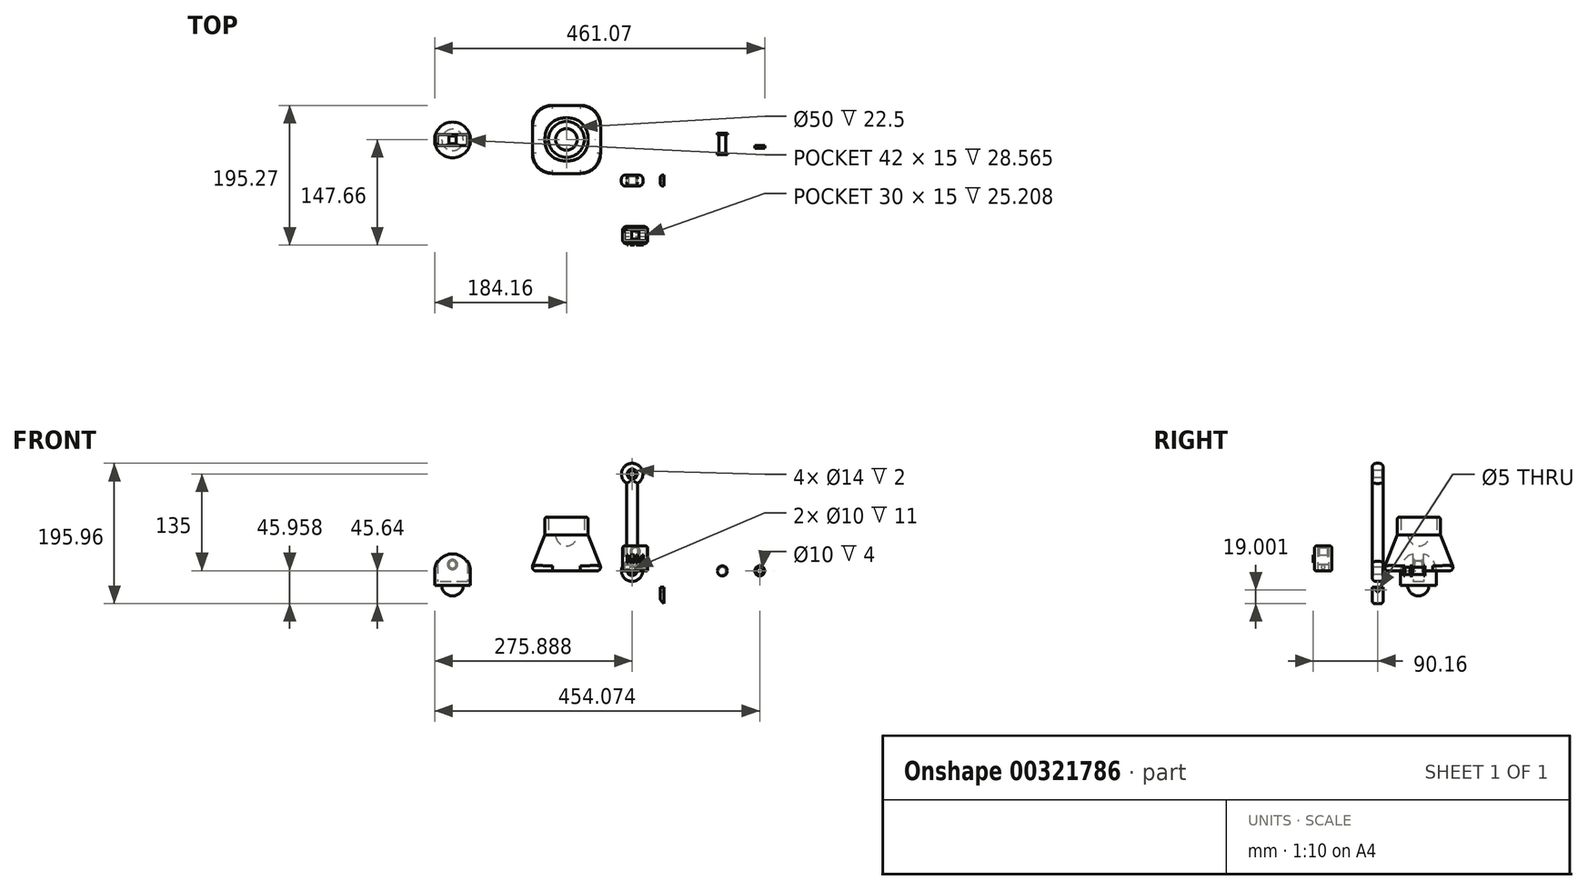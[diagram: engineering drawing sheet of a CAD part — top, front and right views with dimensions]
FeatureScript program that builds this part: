
annotation { "Feature Type Name" : "Feature", "Feature Type Description" : "" }
export const myFeature = defineFeature(function(context is Context, id is Id, definition is map)
    precondition{}
    {
        {
            var Q0;
            Q0=qCreatedBy(makeId("Top.planeOp"),FACE);
            var sketch = newSketch(context, id + "F0", { "sketchPlane" : qUnion([Q0])});
            skLineSegment(sketch, "E0.bottom", {"start": v(0, 0) * mm, "end": v(100, 0) * mm});
            skLineSegment(sketch, "E0.top", {"start": v(0, 100) * mm, "end": v(100, 100) * mm});
            skLineSegment(sketch, "E0.left", {"start": v(0, 0) * mm, "end": v(0, 100) * mm});
            skLineSegment(sketch, "E0.right", {"start": v(100, 0) * mm, "end": v(100, 100) * mm});
            skSolve(sketch);
        }
        {
            var Q0;
            Q0=makeQuery(id+"F0.imprint","IMPRINT",FACE,{"disambiguationData":[TD([[makeQuery(id+"F0.imprint","IMPRINT",EDGE,{"derivedFrom":sQuery(id+"F0.wireOp",EDGE,"E0.bottom")}),1.0]])]});
            cPlane(context, id + "F1", {"entities" : qUnion([Q0]), "cplaneType" : CPlaneType.OFFSET, "offset" : 50 * mm, "width" : 150 * mm, "height" : 150 * mm});
        }
        {
            var Q0;
            Q0=qCreatedBy(id+"F1.planeOp",FACE);
            var sketch = newSketch(context, id + "F2", { "sketchPlane" : qUnion([Q0])});
            skLineSegment(sketch, "E1.bottom", {"start": v(20, 80) * mm, "end": v(80, 80) * mm});
            skLineSegment(sketch, "E1.top", {"start": v(20, 20) * mm, "end": v(80, 20) * mm});
            skLineSegment(sketch, "E1.left", {"start": v(20, 80) * mm, "end": v(20, 20) * mm});
            skLineSegment(sketch, "E1.right", {"start": v(80, 80) * mm, "end": v(80, 20) * mm});
            skSolve(sketch);
        }
        {
            var Q0;
            Q0=makeQuery(id+"F0.imprint","IMPRINT",FACE,{"disambiguationData":[TD([[makeQuery(id+"F0.imprint","IMPRINT",EDGE,{"derivedFrom":sQuery(id+"F0.wireOp",EDGE,"E0.bottom")}),1.0]])]});
            var Q1;
            Q1=makeQuery(id+"F2.imprint","IMPRINT",FACE,{"disambiguationData":[TD([[makeQuery(id+"F2.imprint","IMPRINT",EDGE,{"derivedFrom":sQuery(id+"F2.wireOp",EDGE,"E1.bottom")}),-1.0]])]});
            loft(context, id + "F3", {"sheetProfilesArray" : [{ "sheetProfileEntities" : qUnion([Q0]) }, { "sheetProfileEntities" : qUnion([Q1]) }]});
        }
        {
            var Q0;
            Q0=makeQuery(id+"F3.opLoft","CAP_FACE",FACE,{"disambiguationData":[OSD([makeQuery(id+"F2.imprint","IMPRINT",FACE,{"disambiguationData":[TD([[makeQuery(id+"F2.imprint","IMPRINT",EDGE,{"derivedFrom":sQuery(id+"F2.wireOp",EDGE,"E1.bottom")}),-1.0]])]})])],"isStart":true});
            var sketch = newSketch(context, id + "F4", { "sketchPlane" : qUnion([Q0])});
            skLineSegment(sketch, "E2", {"start": v(50, 65) * mm, "end": v(50, 35) * mm});
            skArc(sketch, "E3", {"start": v(50, 35) * mm, "mid": v(65, 50) * mm, "end": v(50, 65) * mm});
            skPoint(sketch, "E4.orphan", {"position": v(50, 80) * mm});
            skPoint(sketch, "E5.orphan", {"position": v(50, 20) * mm});
            skSolve(sketch);
        }
        {
            var Q0;
            Q0=makeQuery(id+"F4.imprint","IMPRINT",FACE,{"disambiguationData":[TD([[makeQuery(id+"F4.imprint","IMPRINT",EDGE,{"derivedFrom":sQuery(id+"F4.wireOp",EDGE,"E2")}),1.0]])]});
            var Q1;
            Q1=sQuery(id+"F4.wireOp",EDGE,"E2");
            revolve(context, id + "F5", {"operationType" : NewBodyOperationType.REMOVE, "entities" : qUnion([Q0]), "axis" : qUnion([Q1]), "revolveType" : RevolveType.FULL, "oppositeDirection" : true});
        }
        {
            var Q0;
            Q0=makeQuery(id+"F3.opLoft","CAP_FACE",FACE,{"disambiguationData":[OSD([makeQuery(id+"F0.imprint","IMPRINT",FACE,{"disambiguationData":[TD([[makeQuery(id+"F0.imprint","IMPRINT",EDGE,{"derivedFrom":sQuery(id+"F0.wireOp",EDGE,"E0.bottom")}),1.0]])]})])],"isStart":true});
            fillet(context, id + "F6", {"entities" : qUnion([Q0]), "radius" : 5 * mm, "tangentPropagation" : true, "allowEdgeOverflow" : false});
        }
        {
            var Q0;
            Q0=makeQuery(id+"F3.opLoft","SWEPT_EDGE",EDGE,{"disambiguationData":[OSD([sQuery(id+"F0.wireOp",EDGE,"E0.bottom"),sQuery(id+"F0.wireOp",EDGE,"E0.right"),sQuery(id+"F2.wireOp",EDGE,"E1.top"),sQuery(id+"F2.wireOp",EDGE,"E1.right")])]});
            var Q1;
            Q1=makeQuery(id+"F3.opLoft","SWEPT_EDGE",EDGE,{"disambiguationData":[OSD([sQuery(id+"F0.wireOp",EDGE,"E0.top"),sQuery(id+"F0.wireOp",EDGE,"E0.right"),sQuery(id+"F2.wireOp",EDGE,"E1.bottom"),sQuery(id+"F2.wireOp",EDGE,"E1.right")])]});
            var Q2;
            Q2=makeQuery(id+"F3.opLoft","SWEPT_EDGE",EDGE,{"disambiguationData":[OSD([sQuery(id+"F0.wireOp",EDGE,"E0.top"),sQuery(id+"F0.wireOp",EDGE,"E0.left"),sQuery(id+"F2.wireOp",EDGE,"E1.bottom"),sQuery(id+"F2.wireOp",EDGE,"E1.left")])]});
            var Q3;
            Q3=makeQuery(id+"F3.opLoft","SWEPT_EDGE",EDGE,{"disambiguationData":[OSD([sQuery(id+"F0.wireOp",EDGE,"E0.bottom"),sQuery(id+"F0.wireOp",EDGE,"E0.left"),sQuery(id+"F2.wireOp",EDGE,"E1.top"),sQuery(id+"F2.wireOp",EDGE,"E1.left")])]});
            fillet(context, id + "F7", {"entities" : qUnion([Q0, Q1, Q2, Q3]), "radius" : 30 * mm, "tangentPropagation" : true, "allowEdgeOverflow" : false});
        }
        {
            var Q0;
            Q0=qCreatedBy(makeId("Top.planeOp"),FACE);
            var sketch = newSketch(context, id + "F8", { "sketchPlane" : qUnion([Q0])});
            skArc(sketch, "E6", {"start": v(184.89, 22.61) * mm, "mid": v(199.89, 37.61) * mm, "end": v(184.89, 52.61) * mm});
            skLineSegment(sketch, "E7", {"start": v(184.89, 22.61) * mm, "end": v(184.89, 52.61) * mm});
            skSolve(sketch);
        }
        {
            var Q0;
            Q0=qCreatedBy(makeId("Top.planeOp"),FACE);
            cPlane(context, id + "F9", {"entities" : qUnion([Q0]), "cplaneType" : CPlaneType.OFFSET, "offset" : 10 * mm, "width" : 150 * mm, "height" : 150 * mm});
        }
        {
            var Q0;
            Q0=qCreatedBy(id+"F9.planeOp",FACE);
            var sketch = newSketch(context, id + "F10", { "sketchPlane" : qUnion([Q0])});
            skLineSegment(sketch, "E8.bottom", {"start": v(177.39, 45.11) * mm, "end": v(192.39, 45.11) * mm});
            skLineSegment(sketch, "E8.top", {"start": v(177.39, 30.11) * mm, "end": v(192.39, 30.11) * mm});
            skLineSegment(sketch, "E8.left", {"start": v(177.39, 45.11) * mm, "end": v(177.39, 30.11) * mm});
            skLineSegment(sketch, "E8.right", {"start": v(192.39, 45.11) * mm, "end": v(192.39, 30.11) * mm});
            skSolve(sketch);
        }
        {
            var Q0;
            Q0=makeQuery(id+"F8.imprint","IMPRINT",FACE,{"disambiguationData":[TD([[makeQuery(id+"F8.imprint","IMPRINT",EDGE,{"derivedFrom":sQuery(id+"F8.wireOp",EDGE,"E6")}),1.0]])]});
            var Q1;
            Q1=sQuery(id+"F8.wireOp",EDGE,"E7");
            revolve(context, id + "F11", {"entities" : qUnion([Q0]), "axis" : qUnion([Q1]), "revolveType" : RevolveType.FULL});
        }
        {
            var Q0;
            Q0=qSketchRegion(id+"F10",true);
            extrude(context, id + "F12", {"entities" : qUnion([Q0]), "operationType" : NewBodyOperationType.ADD, "depth" : 120 * mm});
        }
        {
            var Q0;
            Q0=makeQuery(id+"F12.boolean.opBoolean","INTERSECT",EDGE,{"derivedFrom":[makeQuery(id+"F11.opRevolve","SWEPT_FACE",FACE,{"disambiguationData":[OSD([sQuery(id+"F8.wireOp",EDGE,"E6")])]}),makeQuery(id+"F12.opExtrude","SWEPT_FACE",FACE,{"disambiguationData":[OSD([sQuery(id+"F10.wireOp",EDGE,"E8.right")])]})]});
            var Q1;
            Q1=makeQuery(id+"F12.boolean.opBoolean","INTERSECT",EDGE,{"derivedFrom":[makeQuery(id+"F11.opRevolve","SWEPT_FACE",FACE,{"disambiguationData":[OSD([sQuery(id+"F8.wireOp",EDGE,"E6")])]}),makeQuery(id+"F12.opExtrude","SWEPT_FACE",FACE,{"disambiguationData":[OSD([sQuery(id+"F10.wireOp",EDGE,"E8.top")])]})]});
            var Q2;
            Q2=makeQuery(id+"F12.boolean.opBoolean","INTERSECT",EDGE,{"derivedFrom":[makeQuery(id+"F11.opRevolve","SWEPT_FACE",FACE,{"disambiguationData":[OSD([sQuery(id+"F8.wireOp",EDGE,"E6")])]}),makeQuery(id+"F12.opExtrude","SWEPT_FACE",FACE,{"disambiguationData":[OSD([sQuery(id+"F10.wireOp",EDGE,"E8.bottom")])]})]});
            var Q3;
            Q3=makeQuery(id+"F12.boolean.opBoolean","INTERSECT",EDGE,{"derivedFrom":[makeQuery(id+"F11.opRevolve","SWEPT_FACE",FACE,{"disambiguationData":[OSD([sQuery(id+"F8.wireOp",EDGE,"E6")])]}),makeQuery(id+"F12.opExtrude","SWEPT_FACE",FACE,{"disambiguationData":[OSD([sQuery(id+"F10.wireOp",EDGE,"E8.left")])]})]});
            var Q4;
            Q4=makeQuery(id+"F12.opExtrude","SWEPT_EDGE",EDGE,{"disambiguationData":[OSD([sQuery(id+"F10.wireOp",EDGE,"E8.bottom"),sQuery(id+"F10.wireOp",EDGE,"E8.left")])]});
            var Q5;
            Q5=makeQuery(id+"F12.opExtrude","SWEPT_EDGE",EDGE,{"disambiguationData":[OSD([sQuery(id+"F10.wireOp",EDGE,"E8.bottom"),sQuery(id+"F10.wireOp",EDGE,"E8.right")])]});
            var Q6;
            Q6=makeQuery(id+"F12.opExtrude","SWEPT_EDGE",EDGE,{"disambiguationData":[OSD([sQuery(id+"F10.wireOp",EDGE,"E8.top"),sQuery(id+"F10.wireOp",EDGE,"E8.right")])]});
            var Q7;
            Q7=makeQuery(id+"F12.opExtrude","SWEPT_EDGE",EDGE,{"disambiguationData":[OSD([sQuery(id+"F10.wireOp",EDGE,"E8.top"),sQuery(id+"F10.wireOp",EDGE,"E8.left")])]});
            fillet(context, id + "F13", {"entities" : qUnion([Q0, Q1, Q2, Q3, Q4, Q5, Q6, Q7]), "radius" : 5 * mm, "tangentPropagation" : true, "allowEdgeOverflow" : false});
        }
        {
            var Q0;
            Q0=makeQuery(id+"F12.opExtrude","CAP_EDGE",EDGE,{"disambiguationData":[OSD([sQuery(id+"F10.wireOp",EDGE,"E8.right")])],"isStart":false});
            cPoint(context, id + "F14", {"entities" : qUnion([Q0]), "parameter" : 0.5});
        }
        {
            var Q0;
            Q0=makeQuery(id+"F12.opExtrude","CAP_EDGE",EDGE,{"disambiguationData":[OSD([sQuery(id+"F10.wireOp",EDGE,"E8.left")])],"isStart":false});
            cPoint(context, id + "F15", {"entities" : qUnion([Q0]), "parameter" : 0.5});
        }
        {
            var Q0;
            {var subQ0=makeQuery(id+"F12.opExtrude","SWEPT_FACE",FACE,{"disambiguationData":[OSD([sQuery(id+"F10.wireOp",EDGE,"E8.left")])]});Q0=makeQuery(id+"F13.opFillet","BLEND_EDGE",EDGE,{"blendedFrom":[makeQuery(id+"F12.boolean.opBoolean","INTERSECT",EDGE,{"derivedFrom":[makeQuery(id+"F11.opRevolve","SWEPT_FACE",FACE,{"disambiguationData":[OSD([sQuery(id+"F8.wireOp",EDGE,"E6")])]}),subQ0]}),subQ0],"blendedInto":[subQ0]});}
            cPoint(context, id + "F16", {"entities" : qUnion([Q0]), "parameter" : 0.5});
        }
        {
            var Q0;
            Q0=qCreatedBy(id+"F14",VERTEX);
            var Q1;
            Q1=qCreatedBy(id+"F15",VERTEX);
            var Q2;
            Q2=qCreatedBy(id+"F16",VERTEX);
            cPlane(context, id + "F17", {"entities" : qUnion([Q0, Q1, Q2]), "cplaneType" : CPlaneType.THREE_POINT, "offset" : 25 * mm, "width" : 150 * mm, "height" : 150 * mm});
        }
        {
            var Q0;
            Q0=qCreatedBy(id+"F17.planeOp",FACE);
            var sketch = newSketch(context, id + "F18", { "sketchPlane" : qUnion([Q0])});
            skCircle(sketch, "E9", {"center": v(-184.89, 137.5) * mm, "radius": 15 * mm});
            skSolve(sketch);
        }
        {
            var Q0;
            Q0=makeQuery(id+"F18.imprint","IMPRINT",FACE,{"disambiguationData":[TD([[makeQuery(id+"F18.imprint","IMPRINT",EDGE,{"derivedFrom":sQuery(id+"F18.wireOp",EDGE,"E9")}),1.0]])]});
            extrude(context, id + "F19", {"entities" : qUnion([Q0]), "operationType" : NewBodyOperationType.ADD, "endBound" : BoundingType.SYMMETRIC, "depth" : 15 * mm});
        }
        {
            var Q0;
            Q0=makeQuery(id+"F19.opExtrude","CAP_EDGE",EDGE,{"disambiguationData":[OSD([sQuery(id+"F18.wireOp",EDGE,"E9")])],"isStart":true});
            var Q1;
            Q1=makeQuery(id+"F19.opExtrude","CAP_EDGE",EDGE,{"disambiguationData":[OSD([sQuery(id+"F18.wireOp",EDGE,"E9")])],"isStart":false});
            fillet(context, id + "F20", {"entities" : qUnion([Q0, Q1]), "radius" : 5 * mm, "tangentPropagation" : true, "allowEdgeOverflow" : false});
        }
        {
            var Q0;
            Q0=makeQuery(id+"F19.boolean.opBoolean","MERGE",FACE,{"derivedFrom":[makeQuery(id+"F12.opExtrude","SWEPT_FACE",FACE,{"disambiguationData":[OSD([sQuery(id+"F10.wireOp",EDGE,"E8.top")])]}),makeQuery(id+"F19.opExtrude","CAP_FACE",FACE,{"disambiguationData":[OSD([sQuery(id+"F18.wireOp",EDGE,"E9")])],"isStart":true})]});
            var sketch = newSketch(context, id + "F21", { "sketchPlane" : qUnion([Q0])});
            skCircle(sketch, "E10", {"center": v(184.89, 137.5) * mm, "radius": 5 * mm});
            skCircle(sketch, "E11", {"center": v(184.89, 137.5) * mm, "radius": 7 * mm});
            skSolve(sketch);
        }
        {
            var Q0;
            Q0=sQuery(id+"F21.wireOp",VERTEX,"E10.center");
            var Q1;
            Q1=makeQuery(id+"F11.opRevolve","SWEPT_BODY",BODY,{"disambiguationData":[OSD([sQuery(id+"F8.wireOp",EDGE,"E6"),sQuery(id+"F8.wireOp",EDGE,"E7")])]});
            hole(context, id + "F22", {"style" : HoleStyle.SIMPLE, "endStyle" : HoleEndStyle.THROUGH, "holeDiameter" : 10 * mm, "tappedDepth" : 12 * mm, "tapClearance" : 3, "locations" : qUnion([Q0]), "scope" : qUnion([Q1])});
        }
        {
            var Q0;
            Q0=makeQuery(id+"F19.boolean.opBoolean","MERGE",FACE,{"derivedFrom":[makeQuery(id+"F12.opExtrude","SWEPT_FACE",FACE,{"disambiguationData":[OSD([sQuery(id+"F10.wireOp",EDGE,"E8.bottom")])]}),makeQuery(id+"F19.opExtrude","CAP_FACE",FACE,{"disambiguationData":[OSD([sQuery(id+"F18.wireOp",EDGE,"E9")])],"isStart":false})]});
            var sketch = newSketch(context, id + "F23", { "sketchPlane" : qUnion([Q0])});
            skCircle(sketch, "E12", {"center": v(-184.89, 137.5) * mm, "radius": 7 * mm});
            skSolve(sketch);
        }
        {
            var Q0;
            Q0=qSketchRegion(id+"F21",true);
            var Q1;
            Q1=qSketchRegion(id+"F23",true);
            extrude(context, id + "F24", {"entities" : qUnion([Q0, Q1]), "operationType" : NewBodyOperationType.REMOVE, "oppositeDirection" : true, "depth" : 2 * mm, "hasSecondDirection" : true, "secondDirectionOppositeDirection" : false, "secondDirectionDepth" : 2 * mm});
        }
        {
            var Q0;
            Q0=qCreatedBy(makeId("Top.planeOp"),FACE);
            var sketch = newSketch(context, id + "F25", { "sketchPlane" : qUnion([Q0])});
            skLineSegment(sketch, "E13.bottom", {"start": v(267.71, 58.7) * mm, "end": v(272.71, 58.7) * mm});
            skLineSegment(sketch, "E13.top", {"start": v(267.71, 28.7) * mm, "end": v(272.71, 28.7) * mm});
            skLineSegment(sketch, "E13.left", {"start": v(267.71, 58.7) * mm, "end": v(267.71, 28.7) * mm});
            skLineSegment(sketch, "E13.right", {"start": v(272.71, 56.7) * mm, "end": v(272.71, 30.7) * mm});
            skLineSegment(sketch, "E14.bottom", {"start": v(272.71, 58.7) * mm, "end": v(274.71, 58.7) * mm});
            skLineSegment(sketch, "E14.top", {"start": v(272.71, 56.7) * mm, "end": v(274.71, 56.7) * mm});
            skLineSegment(sketch, "E14.right", {"start": v(274.71, 58.7) * mm, "end": v(274.71, 56.7) * mm});
            skLineSegment(sketch, "E15.bottom", {"start": v(272.71, 28.7) * mm, "end": v(274.71, 28.7) * mm});
            skLineSegment(sketch, "E15.top", {"start": v(272.71, 30.7) * mm, "end": v(274.71, 30.7) * mm});
            skLineSegment(sketch, "E15.right", {"start": v(274.71, 28.7) * mm, "end": v(274.71, 30.7) * mm});
            skSolve(sketch);
        }
        {
            var Q0;
            Q0=makeQuery(id+"F25.imprint","IMPRINT",FACE,{"disambiguationData":[TD([[makeQuery(id+"F25.imprint","IMPRINT",EDGE,{"derivedFrom":sQuery(id+"F25.wireOp",EDGE,"E13.bottom")}),-1.0]])]});
            var Q1;
            Q1=sQuery(id+"F25.wireOp",EDGE,"E13.left");
            revolve(context, id + "F26", {"entities" : qUnion([Q0]), "axis" : qUnion([Q1]), "revolveType" : RevolveType.FULL});
        }
        {
            var Q0;
            Q0=qCreatedBy(id+"F17.planeOp",FACE);
            var sketch = newSketch(context, id + "F27", { "sketchPlane" : qUnion([Q0])});
            skCircle(sketch, "E16", {"center": v(-319.91, 0) * mm, "radius": 7 * mm});
            skCircle(sketch, "E17", {"center": v(-319.91, 0) * mm, "radius": 5 * mm});
            skSolve(sketch);
        }
        {
            var Q0;
            Q0=qSketchRegion(id+"F27",true);
            extrude(context, id + "F28", {"entities" : qUnion([Q0]), "depth" : 4 * mm});
        }
        {
            var Q0;
            Q0=qCreatedBy(makeId("Top.planeOp"),FACE);
            var sketch = newSketch(context, id + "F29", { "sketchPlane" : qUnion([Q0])});
            skArc(sketch, "E18", {"start": v(-109.16, 24.23) * mm, "mid": v(-84.16, 49.23) * mm, "end": v(-109.16, 74.23) * mm});
            skLineSegment(sketch, "E19", {"start": v(-109.16, 74.23) * mm, "end": v(-109.16, 24.23) * mm});
            skSolve(sketch);
        }
        {
            var Q0;
            Q0=makeQuery(id+"F29.imprint","IMPRINT",FACE,{"disambiguationData":[TD([[makeQuery(id+"F29.imprint","IMPRINT",EDGE,{"derivedFrom":sQuery(id+"F29.wireOp",EDGE,"E18")}),1.0]])]});
            var Q1;
            Q1=sQuery(id+"F29.wireOp",EDGE,"E19");
            revolve(context, id + "F30", {"entities" : qUnion([Q0]), "axis" : qUnion([Q1]), "revolveType" : RevolveType.ONE_DIRECTION, "angle" : 180 * degree});
        }
        {
            var Q0;
            Q0=qCreatedBy(makeId("Front.planeOp"),FACE);
            var sketch = newSketch(context, id + "F31", { "sketchPlane" : qUnion([Q0])});
            skLineSegment(sketch, "E20.left", {"start": v(134.23, 122.33) * mm, "end": v(134.23, 13.3) * mm});
            skLineSegment(sketch, "E20.right", {"start": v(149.23, 122.33) * mm, "end": v(149.23, 13.3) * mm});
            skArc(sketch, "E21", {"start": v(149.23, 122.33) * mm, "mid": v(141.73, 150.32) * mm, "end": v(134.23, 122.33) * mm});
            skArc(sketch, "E22", {"start": v(134.23, 13.3) * mm, "mid": v(141.73, -14.68) * mm, "end": v(149.23, 13.3) * mm});
            skSolve(sketch);
        }
        {
            var Q0;
            Q0=makeQuery(id+"F31.imprint","IMPRINT",FACE,{"disambiguationData":[TD([[makeQuery(id+"F31.imprint","IMPRINT",EDGE,{"derivedFrom":sQuery(id+"F31.wireOp",EDGE,"E20.left")}),1.0]])]});
            extrude(context, id + "F32", {"entities" : qUnion([Q0]), "depth" : 15 * mm});
        }
        {
            var Q0;
            Q0=makeQuery(id+"F32.opExtrude","CAP_FACE",FACE,{"disambiguationData":[OSD([sQuery(id+"F31.wireOp",EDGE,"E20.left"),sQuery(id+"F31.wireOp",EDGE,"E20.right"),sQuery(id+"F31.wireOp",EDGE,"E21"),sQuery(id+"F31.wireOp",EDGE,"E22")])],"isStart":false});
            var Q1;
            Q1=makeQuery(id+"F32.opExtrude","CAP_FACE",FACE,{"disambiguationData":[OSD([sQuery(id+"F31.wireOp",EDGE,"E20.left"),sQuery(id+"F31.wireOp",EDGE,"E20.right"),sQuery(id+"F31.wireOp",EDGE,"E21"),sQuery(id+"F31.wireOp",EDGE,"E22")])],"isStart":true});
            fillet(context, id + "F33", {"entities" : qUnion([Q0, Q1]), "radius" : 5 * mm, "tangentPropagation" : true, "allowEdgeOverflow" : false});
        }
        {
            var Q0;
            Q0=makeQuery(id+"F32.opExtrude","CAP_FACE",FACE,{"disambiguationData":[OSD([sQuery(id+"F31.wireOp",EDGE,"E20.left"),sQuery(id+"F31.wireOp",EDGE,"E20.right"),sQuery(id+"F31.wireOp",EDGE,"E21"),sQuery(id+"F31.wireOp",EDGE,"E22")])],"isStart":false});
            var sketch = newSketch(context, id + "F34", { "sketchPlane" : qUnion([Q0])});
            skCircle(sketch, "E23", {"center": v(141.73, 135.32) * mm, "radius": 5 * mm});
            skCircle(sketch, "E24", {"center": v(141.73, 0.32) * mm, "radius": 5 * mm});
            skCircle(sketch, "E25", {"center": v(141.73, 135.32) * mm, "radius": 7 * mm});
            skCircle(sketch, "E26", {"center": v(141.73, 0.32) * mm, "radius": 7 * mm});
            skSolve(sketch);
        }
        {
            var Q0;
            Q0=makeQuery(id+"F34.imprint","IMPRINT",FACE,{"disambiguationData":[TD([[makeQuery(id+"F34.imprint","IMPRINT",EDGE,{"derivedFrom":sQuery(id+"F34.wireOp",EDGE,"E23")}),1.0]])]});
            var Q1;
            Q1=makeQuery(id+"F34.imprint","IMPRINT",FACE,{"disambiguationData":[TD([[makeQuery(id+"F34.imprint","IMPRINT",EDGE,{"derivedFrom":sQuery(id+"F34.wireOp",EDGE,"E24")}),1.0]])]});
            extrude(context, id + "F35", {"entities" : qUnion([Q0, Q1]), "operationType" : NewBodyOperationType.REMOVE, "endBound" : BoundingType.THROUGH_ALL, "oppositeDirection" : true, "depth" : 25 * mm});
        }
        {
            var Q0;
            Q0=qSketchRegion(id+"F34",true);
            extrude(context, id + "F36", {"entities" : qUnion([Q0]), "operationType" : NewBodyOperationType.REMOVE, "oppositeDirection" : true, "depth" : 2 * mm});
        }
        {
            var Q0;
            Q0=makeQuery(id+"F32.opExtrude","CAP_FACE",FACE,{"disambiguationData":[OSD([sQuery(id+"F31.wireOp",EDGE,"E20.left"),sQuery(id+"F31.wireOp",EDGE,"E20.right"),sQuery(id+"F31.wireOp",EDGE,"E21"),sQuery(id+"F31.wireOp",EDGE,"E22")])],"isStart":true});
            var sketch = newSketch(context, id + "F37", { "sketchPlane" : qUnion([Q0])});
            skCircle(sketch, "E27", {"center": v(-141.73, 135.32) * mm, "radius": 7 * mm});
            skCircle(sketch, "E28", {"center": v(-141.73, 0.32) * mm, "radius": 7 * mm});
            skSolve(sketch);
        }
        {
            var Q0;
            Q0=qSketchRegion(id+"F37",true);
            extrude(context, id + "F38", {"entities" : qUnion([Q0]), "operationType" : NewBodyOperationType.REMOVE, "oppositeDirection" : true, "depth" : 2 * mm});
        }
        {
            var Q0;
            Q0=makeQuery(id+"F30.opRevolve","CAP_FACE",FACE,{"disambiguationData":[OSD([sQuery(id+"F29.wireOp",EDGE,"E18"),sQuery(id+"F29.wireOp",EDGE,"E19")])],"isStart":true});
            var sketch = newSketch(context, id + "F39", { "sketchPlane" : qUnion([Q0])});
            skLineSegment(sketch, "E29.bottom", {"start": v(-88.16, -56.73) * mm, "end": v(-130.16, -56.73) * mm});
            skLineSegment(sketch, "E29.top", {"start": v(-88.16, -41.73) * mm, "end": v(-130.16, -41.73) * mm});
            skLineSegment(sketch, "E29.left", {"start": v(-88.16, -56.73) * mm, "end": v(-88.16, -41.73) * mm});
            skLineSegment(sketch, "E29.right", {"start": v(-130.16, -56.73) * mm, "end": v(-130.16, -41.73) * mm});
            skSolve(sketch);
        }
        {
            var Q0;
            Q0=makeQuery(id+"F39.imprint","IMPRINT",FACE,{"disambiguationData":[TD([[makeQuery(id+"F39.imprint","IMPRINT",EDGE,{"derivedFrom":sQuery(id+"F39.wireOp",EDGE,"E29.bottom")}),1.0]])]});
            var Q1;
            Q1=makeQuery(id+"F39.imprint","IMPRINT",FACE,{"disambiguationData":[TD([[makeQuery(id+"F39.imprint","IMPRINT",EDGE,{"derivedFrom":sQuery(id+"F39.wireOp",EDGE,"E29.bottom")}),-1.0]])]});
            extrude(context, id + "F40", {"entities" : qUnion([Q0, Q1]), "operationType" : NewBodyOperationType.ADD, "depth" : 20 * mm});
        }
        {
            var Q0;
            Q0=makeQuery(id+"F40.opExtrude","CAP_FACE",FACE,{"disambiguationData":[OSD([sQuery(id+"F29.wireOp",EDGE,"E18")])],"isStart":false});
            var sketch = newSketch(context, id + "F41", { "sketchPlane" : qUnion([Q0])});
            skArc(sketch, "E30", {"start": v(-109.16, -34.23) * mm, "mid": v(-124.16, -49.23) * mm, "end": v(-109.16, -64.23) * mm});
            skLineSegment(sketch, "E31", {"start": v(-109.16, -64.23) * mm, "end": v(-109.16, -34.23) * mm});
            skSolve(sketch);
        }
        {
            var Q0;
            Q0=makeQuery(id+"F41.imprint","IMPRINT",FACE,{"disambiguationData":[TD([[makeQuery(id+"F41.imprint","IMPRINT",EDGE,{"derivedFrom":sQuery(id+"F41.wireOp",EDGE,"E30")}),1.0]])]});
            var Q1;
            Q1=sQuery(id+"F41.wireOp",EDGE,"E31");
            revolve(context, id + "F42", {"operationType" : NewBodyOperationType.ADD, "entities" : qUnion([Q0]), "axis" : qUnion([Q1]), "revolveType" : RevolveType.FULL});
        }
        {
            var Q0;
            Q0=qSketchRegion(id+"F39",true);
            extrude(context, id + "F43", {"entities" : qUnion([Q0]), "operationType" : NewBodyOperationType.REMOVE, "endBound" : BoundingType.THROUGH_ALL, "oppositeDirection" : true, "depth" : 25 * mm, "hasSecondDirection" : true, "secondDirectionOppositeDirection" : false, "secondDirectionDepth" : 15 * mm});
        }
        {
            var Q0;
            Q0=makeQuery(id+"F43.boolean.opBoolean","COPY",FACE,{"derivedFrom":makeQuery(id+"F43.opExtrude","SWEPT_FACE",FACE,{"disambiguationData":[OSD([sQuery(id+"F39.wireOp",EDGE,"E29.top")])]})});
            var sketch = newSketch(context, id + "F44", { "sketchPlane" : qUnion([Q0])});
            skCircle(sketch, "E32", {"center": v(109.16, 8.85) * mm, "radius": 7 * mm});
            skPoint(sketch, "E32.centerSnap0", {"position": v(109.16, 23.85) * mm});
            skPoint(sketch, "E32.centerSnap1", {"position": v(130.16, -1.85) * mm});
            skSolve(sketch);
        }
        {
            var Q0;
            Q0=makeQuery(id+"F44.imprint","IMPRINT",FACE,{"disambiguationData":[TD([[makeQuery(id+"F44.imprint","IMPRINT",EDGE,{"derivedFrom":sQuery(id+"F44.wireOp",EDGE,"E32")}),1.0]])]});
            extrude(context, id + "F45", {"entities" : qUnion([Q0]), "operationType" : NewBodyOperationType.ADD, "depth" : 2 * mm});
        }
        {
            var Q0;
            Q0=makeQuery(id+"F45.opExtrude","CAP_FACE",FACE,{"disambiguationData":[OSD([sQuery(id+"F44.wireOp",EDGE,"E32")])],"isStart":false});
            var sketch = newSketch(context, id + "F46", { "sketchPlane" : qUnion([Q0])});
            skCircle(sketch, "E33", {"center": v(109.16, 8.85) * mm, "radius": 5 * mm});
            skSolve(sketch);
        }
        {
            var Q0;
            Q0=makeQuery(id+"F46.imprint","IMPRINT",FACE,{"disambiguationData":[TD([[makeQuery(id+"F46.imprint","IMPRINT",EDGE,{"derivedFrom":sQuery(id+"F46.wireOp",EDGE,"E33")}),1.0]])]});
            extrude(context, id + "F47", {"entities" : qUnion([Q0]), "operationType" : NewBodyOperationType.ADD, "endBound" : BoundingType.UP_TO_NEXT, "depth" : 25 * mm});
        }
        {
            var Q0;
            Q0=qCreatedBy(makeId("Top.planeOp"),FACE);
            var sketch = newSketch(context, id + "F48", { "sketchPlane" : qUnion([Q0])});
            skLineSegment(sketch, "E34.bottom", {"start": v(203.21, -84.7) * mm, "end": v(208.21, -84.7) * mm});
            skLineSegment(sketch, "E34.top", {"start": v(203.21, -99.7) * mm, "end": v(208.21, -99.7) * mm});
            skLineSegment(sketch, "E34.left", {"start": v(198.21, -89.7) * mm, "end": v(198.21, -94.7) * mm});
            skLineSegment(sketch, "E34.right", {"start": v(213.21, -89.7) * mm, "end": v(213.21, -94.7) * mm});
            skPoint(sketch, "E35.visualSharp", {"position": v(198.21, -84.7) * mm});
            skArc(sketch, "E35.filletArc", {"start": v(203.21, -84.7) * mm, "mid": v(199.68, -86.16) * mm, "end": v(198.21, -89.7) * mm});
            skPoint(sketch, "E36.visualSharp", {"position": v(213.21, -84.7) * mm});
            skArc(sketch, "E36.filletArc", {"start": v(213.21, -89.7) * mm, "mid": v(211.75, -86.16) * mm, "end": v(208.21, -84.7) * mm});
            skPoint(sketch, "E37.visualSharp", {"position": v(213.21, -99.7) * mm});
            skArc(sketch, "E37.filletArc", {"start": v(208.21, -99.7) * mm, "mid": v(211.75, -98.23) * mm, "end": v(213.21, -94.7) * mm});
            skPoint(sketch, "E38.visualSharp", {"position": v(198.21, -99.7) * mm});
            skArc(sketch, "E38.filletArc", {"start": v(198.21, -94.7) * mm, "mid": v(199.68, -98.23) * mm, "end": v(203.21, -99.7) * mm});
            skLineSegment(sketch, "E39.bottom", {"start": v(192.71, -74.2) * mm, "end": v(218.71, -74.2) * mm});
            skLineSegment(sketch, "E39.top", {"start": v(192.71, -110.2) * mm, "end": v(218.71, -110.2) * mm});
            skLineSegment(sketch, "E39.left", {"start": v(187.71, -79.2) * mm, "end": v(187.71, -105.2) * mm});
            skLineSegment(sketch, "E39.right", {"start": v(223.71, -79.2) * mm, "end": v(223.71, -105.2) * mm});
            skPoint(sketch, "E40.visualSharp", {"position": v(187.71, -74.2) * mm});
            skArc(sketch, "E40.filletArc", {"start": v(192.71, -74.2) * mm, "mid": v(189.18, -75.66) * mm, "end": v(187.71, -79.2) * mm});
            skPoint(sketch, "E41.visualSharp", {"position": v(223.71, -74.2) * mm});
            skArc(sketch, "E41.filletArc", {"start": v(223.71, -79.2) * mm, "mid": v(222.25, -75.66) * mm, "end": v(218.71, -74.2) * mm});
            skPoint(sketch, "E42.visualSharp", {"position": v(223.71, -110.2) * mm});
            skArc(sketch, "E42.filletArc", {"start": v(218.71, -110.2) * mm, "mid": v(222.25, -108.73) * mm, "end": v(223.71, -105.2) * mm});
            skPoint(sketch, "E43.visualSharp", {"position": v(187.71, -110.2) * mm});
            skArc(sketch, "E43.filletArc", {"start": v(187.71, -105.2) * mm, "mid": v(189.18, -108.73) * mm, "end": v(192.71, -110.2) * mm});
            skSolve(sketch);
        }
        {
            var Q0;
            Q0=makeQuery(id+"F48.imprint","IMPRINT",FACE,{"disambiguationData":[TD([[makeQuery(id+"F48.imprint","IMPRINT",EDGE,{"derivedFrom":sQuery(id+"F48.wireOp",EDGE,"E34.bottom")}),1.0]])]});
            extrude(context, id + "F49", {"entities" : qUnion([Q0]), "depth" : 20 * mm});
        }
        {
            var Q0;
            Q0=makeQuery(id+"F49.opExtrude","CAP_EDGE",EDGE,{"disambiguationData":[OSD([sQuery(id+"F48.wireOp",EDGE,"E39.left")])],"isStart":false});
            fillet(context, id + "F50", {"entities" : qUnion([Q0]), "radius" : 10 * mm, "tangentPropagation" : true, "allowEdgeOverflow" : false});
        }
        {
            var Q0;
            Q0=makeQuery(id+"F49.opExtrude","CAP_EDGE",EDGE,{"disambiguationData":[OSD([sQuery(id+"F48.wireOp",EDGE,"E34.top")])],"isStart":true});
            var Q1;
            Q1=makeQuery(id+"F49.opExtrude","CAP_EDGE",EDGE,{"disambiguationData":[OSD([sQuery(id+"F48.wireOp",EDGE,"E37.filletArc")])],"isStart":true});
            fillet(context, id + "F51", {"entities" : qUnion([Q0, Q1]), "radius" : 5 * mm, "tangentPropagation" : true, "allowEdgeOverflow" : false});
        }
        {
            var Q0;
            Q0=makeQuery(id+"F11.opRevolve","SWEPT_BODY",BODY,{"disambiguationData":[OSD([sQuery(id+"F8.wireOp",EDGE,"E6"),sQuery(id+"F8.wireOp",EDGE,"E7")])]});
            deleteBodies(context, id + "F52", {"entities" : qUnion([Q0])});
        }
        {
            var Q0;
            Q0=makeQuery(id+"F49.opExtrude","SWEPT_BODY",BODY,{"disambiguationData":[OSD([sQuery(id+"F48.wireOp",EDGE,"E34.bottom"),sQuery(id+"F48.wireOp",EDGE,"E34.top"),sQuery(id+"F48.wireOp",EDGE,"E34.left"),sQuery(id+"F48.wireOp",EDGE,"E34.right"),sQuery(id+"F48.wireOp",EDGE,"E35.filletArc"),sQuery(id+"F48.wireOp",EDGE,"E36.filletArc"),sQuery(id+"F48.wireOp",EDGE,"E37.filletArc"),sQuery(id+"F48.wireOp",EDGE,"E38.filletArc"),sQuery(id+"F48.wireOp",EDGE,"E39.bottom"),sQuery(id+"F48.wireOp",EDGE,"E39.top"),sQuery(id+"F48.wireOp",EDGE,"E39.left"),sQuery(id+"F48.wireOp",EDGE,"E39.right"),sQuery(id+"F48.wireOp",EDGE,"E40.filletArc"),sQuery(id+"F48.wireOp",EDGE,"E41.filletArc"),sQuery(id+"F48.wireOp",EDGE,"E42.filletArc"),sQuery(id+"F48.wireOp",EDGE,"E43.filletArc")])]});
            deleteBodies(context, id + "F53", {"entities" : qUnion([Q0])});
        }
        {
            var Q0;
            Q0=makeQuery(id+"F43.boolean.opBoolean","COPY",FACE,{"derivedFrom":makeQuery(id+"F43.opExtrude","SWEPT_FACE",FACE,{"disambiguationData":[OSD([sQuery(id+"F39.wireOp",EDGE,"E29.bottom")])]})});
            var sketch = newSketch(context, id + "F54", { "sketchPlane" : qUnion([Q0])});
            skCircle(sketch, "E44", {"center": v(-109.16, 8.85) * mm, "radius": 7 * mm});
            skSolve(sketch);
        }
        {
            var Q0;
            Q0=makeQuery(id+"F54.imprint","IMPRINT",FACE,{"disambiguationData":[TD([[makeQuery(id+"F54.imprint","IMPRINT",EDGE,{"derivedFrom":sQuery(id+"F54.wireOp",EDGE,"E44")}),1.0]])]});
            extrude(context, id + "F55", {"entities" : qUnion([Q0]), "operationType" : NewBodyOperationType.ADD, "depth" : 2 * mm});
        }
        {
            var Q0;
            Q0=qCreatedBy(makeId("Top.planeOp"),FACE);
            var sketch = newSketch(context, id + "F56", { "sketchPlane" : qUnion([Q0])});
            skLineSegment(sketch, "E45.bottom", {"start": v(133.56, -71.66) * mm, "end": v(158.56, -71.66) * mm});
            skLineSegment(sketch, "E45.top", {"start": v(133.56, -95.66) * mm, "end": v(158.56, -95.66) * mm});
            skLineSegment(sketch, "E45.left", {"start": v(128.56, -76.66) * mm, "end": v(128.56, -90.66) * mm});
            skLineSegment(sketch, "E45.right", {"start": v(163.56, -76.66) * mm, "end": v(163.56, -90.66) * mm});
            skPoint(sketch, "E46.visualSharp", {"position": v(163.56, -71.66) * mm});
            skArc(sketch, "E46.filletArc", {"start": v(163.56, -76.66) * mm, "mid": v(162.1, -73.13) * mm, "end": v(158.56, -71.66) * mm});
            skPoint(sketch, "E47.visualSharp", {"position": v(163.56, -95.66) * mm});
            skArc(sketch, "E47.filletArc", {"start": v(158.56, -95.66) * mm, "mid": v(162.1, -94.2) * mm, "end": v(163.56, -90.66) * mm});
            skPoint(sketch, "E48.visualSharp", {"position": v(128.56, -95.66) * mm});
            skArc(sketch, "E48.filletArc", {"start": v(128.56, -90.66) * mm, "mid": v(130.03, -94.2) * mm, "end": v(133.56, -95.66) * mm});
            skPoint(sketch, "E49.visualSharp", {"position": v(128.56, -71.66) * mm});
            skArc(sketch, "E49.filletArc", {"start": v(133.56, -71.66) * mm, "mid": v(130.03, -73.13) * mm, "end": v(128.56, -76.66) * mm});
            skPoint(sketch, "E50.firstSnap0", {"position": v(146.06, -71.66) * mm});
            skLineSegment(sketch, "E50.bottom", {"start": v(131.06, -76.16) * mm, "end": v(161.06, -76.16) * mm});
            skLineSegment(sketch, "E50.top", {"start": v(131.06, -91.16) * mm, "end": v(161.06, -91.16) * mm});
            skLineSegment(sketch, "E50.left", {"start": v(131.06, -76.16) * mm, "end": v(131.06, -91.16) * mm});
            skLineSegment(sketch, "E50.right", {"start": v(161.06, -76.16) * mm, "end": v(161.06, -91.16) * mm});
            skSolve(sketch);
        }
        {
            var Q0;
            Q0=makeQuery(id+"F56.imprint","IMPRINT",FACE,{"disambiguationData":[TD([[makeQuery(id+"F56.imprint","IMPRINT",EDGE,{"derivedFrom":sQuery(id+"F56.wireOp",EDGE,"E45.bottom")}),-1.0]])]});
            extrude(context, id + "F57", {"entities" : qUnion([Q0]), "depth" : 35 * mm});
        }
        {
            var Q0;
            Q0=makeQuery(id+"F57.opExtrude","SWEPT_FACE",FACE,{"disambiguationData":[OSD([sQuery(id+"F56.wireOp",EDGE,"E50.bottom")])]});
            var sketch = newSketch(context, id + "F58", { "sketchPlane" : qUnion([Q0])});
            skCircle(sketch, "E51", {"center": v(146.06, 27.5) * mm, "radius": 5 * mm});
            skCircle(sketch, "E52", {"center": v(146.06, 27.5) * mm, "radius": 7 * mm});
            skSolve(sketch);
        }
        {
            var Q0;
            Q0=makeQuery(id+"F58.imprint","IMPRINT",FACE,{"disambiguationData":[TD([[makeQuery(id+"F58.imprint","IMPRINT",EDGE,{"derivedFrom":sQuery(id+"F58.wireOp",EDGE,"E51")}),1.0]])]});
            extrude(context, id + "F59", {"entities" : qUnion([Q0]), "operationType" : NewBodyOperationType.ADD, "endBound" : BoundingType.UP_TO_NEXT, "depth" : 25 * mm});
        }
        {
            var Q0;
            Q0=makeQuery(id+"F58.imprint","IMPRINT",FACE,{"disambiguationData":[TD([[makeQuery(id+"F58.imprint","IMPRINT",EDGE,{"derivedFrom":sQuery(id+"F58.wireOp",EDGE,"E51")}),-1.0]])]});
            extrude(context, id + "F60", {"entities" : qUnion([Q0]), "operationType" : NewBodyOperationType.ADD, "depth" : 2 * mm});
        }
        {
            var Q0;
            Q0=makeQuery(id+"F57.opExtrude","SWEPT_FACE",FACE,{"disambiguationData":[OSD([sQuery(id+"F56.wireOp",EDGE,"E50.top")])]});
            var sketch = newSketch(context, id + "F61", { "sketchPlane" : qUnion([Q0])});
            skCircle(sketch, "E53", {"center": v(-146.06, 27.5) * mm, "radius": 7 * mm});
            skSolve(sketch);
        }
        {
            var Q0;
            Q0=makeQuery(id+"F61.imprint","IMPRINT",FACE,{"disambiguationData":[TD([[makeQuery(id+"F61.imprint","IMPRINT",EDGE,{"derivedFrom":sQuery(id+"F61.wireOp",EDGE,"E53")}),1.0]])]});
            extrude(context, id + "F62", {"entities" : qUnion([Q0]), "operationType" : NewBodyOperationType.ADD, "depth" : 2 * mm});
        }
        {
            var Q0;
            Q0=qCreatedBy(makeId("Front.planeOp"),FACE);
            var sketch = newSketch(context, id + "F63", { "sketchPlane" : qUnion([Q0])});
            skLineSegment(sketch, "E54", {"start": v(181.27, -22.64) * mm, "end": v(181.27, -40.64) * mm});
            skLineSegment(sketch, "E55", {"start": v(181.27, -40.64) * mm, "end": v(186.27, -45.64) * mm});
            skLineSegment(sketch, "E56", {"start": v(186.27, -45.64) * mm, "end": v(186.27, -22.64) * mm});
            skLineSegment(sketch, "E57", {"start": v(186.27, -22.64) * mm, "end": v(181.27, -22.64) * mm});
            skSolve(sketch);
        }
        {
            var Q0;
            Q0=makeQuery(id+"F63.imprint","IMPRINT",FACE,{"disambiguationData":[TD([[makeQuery(id+"F63.imprint","IMPRINT",EDGE,{"derivedFrom":sQuery(id+"F63.wireOp",EDGE,"E54")}),1.0]])]});
            extrude(context, id + "F64", {"entities" : qUnion([Q0]), "depth" : 15 * mm});
        }
        {
            var Q0;
            Q0=makeQuery(id+"F57.opExtrude","SWEPT_FACE",FACE,{"disambiguationData":[OSD([sQuery(id+"F56.wireOp",EDGE,"E50.left")])]});
            var sketch = newSketch(context, id + "F65", { "sketchPlane" : qUnion([Q0])});
            skCircle(sketch, "E58", {"center": v(-83.66, 5) * mm, "radius": 2.5 * mm});
            skPoint(sketch, "E58.centerSnap0", {"position": v(-83.66, 0) * mm});
            skLineSegment(sketch, "E59.bottom", {"start": v(-91.16, 9.75) * mm, "end": v(-76.16, 9.75) * mm});
            skLineSegment(sketch, "E59.top", {"start": v(-91.16, 9) * mm, "end": v(-76.16, 9) * mm});
            skLineSegment(sketch, "E59.left", {"start": v(-91.16, 9.75) * mm, "end": v(-91.16, 9) * mm});
            skLineSegment(sketch, "E59.right", {"start": v(-76.16, 9.75) * mm, "end": v(-76.16, 9) * mm});
            skSolve(sketch);
        }
        {
            var Q0;
            Q0=makeQuery(id+"F65.imprint","IMPRINT",FACE,{"disambiguationData":[TD([[makeQuery(id+"F65.imprint","IMPRINT",EDGE,{"derivedFrom":sQuery(id+"F65.wireOp",EDGE,"E58")}),1.0]])]});
            var Q1;
            Q1=makeQuery(id+"F65.imprint","IMPRINT",FACE,{"disambiguationData":[TD([[makeQuery(id+"F65.imprint","IMPRINT",EDGE,{"derivedFrom":sQuery(id+"F65.wireOp",EDGE,"E59.bottom")}),-1.0]])]});
            extrude(context, id + "F66", {"entities" : qUnion([Q0, Q1]), "operationType" : NewBodyOperationType.ADD, "endBound" : BoundingType.UP_TO_NEXT, "depth" : 25 * mm});
        }
        {
            var Q0;
            Q0=makeQuery(id+"F64.opExtrude","SWEPT_FACE",FACE,{"disambiguationData":[OSD([sQuery(id+"F63.wireOp",EDGE,"E56")])]});
            var sketch = newSketch(context, id + "F67", { "sketchPlane" : qUnion([Q0])});
            skCircle(sketch, "E60", {"center": v(-7.5, -26.64) * mm, "radius": 2.5 * mm});
            skPoint(sketch, "E60.centerSnap0", {"position": v(-7.5, -22.64) * mm});
            skSolve(sketch);
        }
        {
            var Q0;
            Q0=makeQuery(id+"F67.imprint","IMPRINT",FACE,{"disambiguationData":[TD([[makeQuery(id+"F67.imprint","IMPRINT",EDGE,{"derivedFrom":sQuery(id+"F67.wireOp",EDGE,"E60")}),1.0]])]});
            extrude(context, id + "F68", {"entities" : qUnion([Q0]), "operationType" : NewBodyOperationType.REMOVE, "endBound" : BoundingType.UP_TO_NEXT, "oppositeDirection" : true, "depth" : 25 * mm});
        }
        {
            var Q0;
            Q0=makeQuery(id+"F57.opExtrude","CAP_EDGE",EDGE,{"disambiguationData":[OSD([sQuery(id+"F56.wireOp",EDGE,"E45.top")])],"isStart":true});
            var Q1;
            Q1=makeQuery(id+"F57.opExtrude","CAP_EDGE",EDGE,{"disambiguationData":[OSD([sQuery(id+"F56.wireOp",EDGE,"E45.right")])],"isStart":true});
            var Q2;
            Q2=makeQuery(id+"F57.opExtrude","CAP_EDGE",EDGE,{"disambiguationData":[OSD([sQuery(id+"F56.wireOp",EDGE,"E47.filletArc")])],"isStart":true});
            var Q3;
            Q3=makeQuery(id+"F57.opExtrude","CAP_EDGE",EDGE,{"disambiguationData":[OSD([sQuery(id+"F56.wireOp",EDGE,"E45.bottom")])],"isStart":true});
            var Q4;
            Q4=makeQuery(id+"F57.opExtrude","CAP_EDGE",EDGE,{"disambiguationData":[OSD([sQuery(id+"F56.wireOp",EDGE,"E49.filletArc")])],"isStart":true});
            var Q5;
            Q5=makeQuery(id+"F57.opExtrude","CAP_EDGE",EDGE,{"disambiguationData":[OSD([sQuery(id+"F56.wireOp",EDGE,"E45.left")])],"isStart":true});
            var Q6;
            Q6=makeQuery(id+"F57.opExtrude","CAP_EDGE",EDGE,{"disambiguationData":[OSD([sQuery(id+"F56.wireOp",EDGE,"E48.filletArc")])],"isStart":true});
            var Q7;
            Q7=makeQuery(id+"F57.opExtrude","CAP_EDGE",EDGE,{"disambiguationData":[OSD([sQuery(id+"F56.wireOp",EDGE,"E46.filletArc")])],"isStart":true});
            fillet(context, id + "F69", {"entities" : qUnion([Q0, Q1, Q2, Q3, Q4, Q5, Q6, Q7]), "radius" : 2 * mm, "tangentPropagation" : true, "allowEdgeOverflow" : false});
        }
        {
            var Q0;
            Q0=makeQuery(id+"F57.opExtrude","CAP_EDGE",EDGE,{"disambiguationData":[OSD([sQuery(id+"F56.wireOp",EDGE,"E45.top")])],"isStart":false});
            var Q1;
            Q1=makeQuery(id+"F57.opExtrude","CAP_EDGE",EDGE,{"disambiguationData":[OSD([sQuery(id+"F56.wireOp",EDGE,"E46.filletArc")])],"isStart":false});
            var Q2;
            Q2=makeQuery(id+"F57.opExtrude","CAP_EDGE",EDGE,{"disambiguationData":[OSD([sQuery(id+"F56.wireOp",EDGE,"E47.filletArc")])],"isStart":false});
            var Q3;
            Q3=makeQuery(id+"F57.opExtrude","CAP_EDGE",EDGE,{"disambiguationData":[OSD([sQuery(id+"F56.wireOp",EDGE,"E48.filletArc")])],"isStart":false});
            var Q4;
            Q4=makeQuery(id+"F57.opExtrude","CAP_EDGE",EDGE,{"disambiguationData":[OSD([sQuery(id+"F56.wireOp",EDGE,"E45.left")])],"isStart":false});
            var Q5;
            Q5=makeQuery(id+"F57.opExtrude","CAP_EDGE",EDGE,{"disambiguationData":[OSD([sQuery(id+"F56.wireOp",EDGE,"E45.bottom")])],"isStart":false});
            var Q6;
            Q6=makeQuery(id+"F57.opExtrude","CAP_EDGE",EDGE,{"disambiguationData":[OSD([sQuery(id+"F56.wireOp",EDGE,"E49.filletArc")])],"isStart":false});
            fillet(context, id + "F70", {"entities" : qUnion([Q0, Q1, Q2, Q3, Q4, Q5, Q6]), "radius" : 3 * mm, "tangentPropagation" : true, "allowEdgeOverflow" : false});
        }
        {
            var Q0;
            Q0=makeQuery(id+"F64.opExtrude","CAP_EDGE",EDGE,{"disambiguationData":[OSD([sQuery(id+"F63.wireOp",EDGE,"E55")])],"isStart":false});
            var Q1;
            Q1=makeQuery(id+"F64.opExtrude","CAP_EDGE",EDGE,{"disambiguationData":[OSD([sQuery(id+"F63.wireOp",EDGE,"E55")])],"isStart":true});
            var Q2;
            Q2=makeQuery(id+"F64.opExtrude","SWEPT_EDGE",EDGE,{"disambiguationData":[OSD([sQuery(id+"F63.wireOp",EDGE,"E54"),sQuery(id+"F63.wireOp",EDGE,"E55")])]});
            var Q3;
            Q3=makeQuery(id+"F64.opExtrude","CAP_EDGE",EDGE,{"disambiguationData":[OSD([sQuery(id+"F63.wireOp",EDGE,"E54")])],"isStart":false});
            var Q4;
            Q4=makeQuery(id+"F64.opExtrude","CAP_EDGE",EDGE,{"disambiguationData":[OSD([sQuery(id+"F63.wireOp",EDGE,"E54")])],"isStart":true});
            fillet(context, id + "F71", {"entities" : qUnion([Q0, Q1, Q2, Q3, Q4]), "radius" : 3 * mm, "tangentPropagation" : true, "allowEdgeOverflow" : false});
        }
        {
            var Q0;
            Q0=makeQuery(id+"F3.opLoft","CAP_FACE",FACE,{"disambiguationData":[OSD([makeQuery(id+"F2.imprint","IMPRINT",FACE,{"disambiguationData":[TD([[makeQuery(id+"F2.imprint","IMPRINT",EDGE,{"derivedFrom":sQuery(id+"F2.wireOp",EDGE,"E1.bottom")}),-1.0]])]})])],"isStart":true});
            var sketch = newSketch(context, id + "F72", { "sketchPlane" : qUnion([Q0])});
            skCircle(sketch, "E61", {"center": v(50, 50) * mm, "radius": 25 * mm});
            skSolve(sketch);
        }
        {
            var Q0;
            Q0=makeQuery(id+"F72.imprint","IMPRINT",FACE,{"disambiguationData":[TD([[makeQuery(id+"F72.imprint","IMPRINT",EDGE,{"derivedFrom":sQuery(id+"F72.wireOp",EDGE,"E61")}),-1.0]])]});
            extrude(context, id + "F73", {"entities" : qUnion([Q0]), "operationType" : NewBodyOperationType.ADD, "depth" : 25 * mm});
        }
        {
            var Q0;
            {var subQ0=sQuery(id+"F2.wireOp",EDGE,"E1.bottom");var subQ1=sQuery(id+"F2.wireOp",EDGE,"E1.top");var subQ2=sQuery(id+"F2.wireOp",EDGE,"E1.left");var subQ3=sQuery(id+"F2.wireOp",EDGE,"E1.right");Q0=makeQuery(id+"F73.opExtrude","CAP_FACE",FACE,{"disambiguationData":[OSD([sQuery(id+"F0.wireOp",EDGE,"E0.bottom"),sQuery(id+"F0.wireOp",EDGE,"E0.top"),sQuery(id+"F0.wireOp",EDGE,"E0.left"),sQuery(id+"F0.wireOp",EDGE,"E0.right"),subQ0,subQ1,subQ2,subQ3,makeQuery(id+"F2.imprint","IMPRINT",FACE,{"disambiguationData":[TD([[makeQuery(id+"F2.imprint","IMPRINT",EDGE,{"derivedFrom":subQ0}),-1.0]])]}),sQuery(id+"F72.wireOp",EDGE,"E61")])],"isStart":false});}
            fillet(context, id + "F74", {"entities" : qUnion([Q0]), "radius" : 2.5 * mm, "tangentPropagation" : true, "allowEdgeOverflow" : false});
        }
        {
            var Q0;
            Q0=makeQuery(id+"F57.opExtrude","SWEPT_FACE",FACE,{"disambiguationData":[OSD([sQuery(id+"F56.wireOp",EDGE,"E45.top")])]});
            var sketch = newSketch(context, id + "F75", { "sketchPlane" : qUnion([Q0])});
            skText(sketch, "E62", { "text": "IEM\n\n", "fontName": "OpenSans-Regular.ttf"});
            const initialGuessF75  = {"E62": [0.13356, 0.01172, 1, 0, 0.01056]};
            skSetInitialGuess(sketch, initialGuessF75);
            skSolve(sketch);
        }
        {
            var Q0;
            Q0=qSketchRegion(id+"F75",true);
            extrude(context, id + "F76", {"entities" : qUnion([Q0]), "operationType" : NewBodyOperationType.ADD, "depth" : 2 * mm});
        }
    });
